# Revit family: Resideo_ThermostaticRadiatorValve_V2100Lsss
name_source: partatom
category: Pipe Accessories
units: mm (PartAtom-declared; Revit-internal decimal feet)

## family parameters
Always vertical = Yes
Cut with Voids When Loaded = No
OmniClass Number = 23.65.55.00
OmniClass Title = Distribution of Supplied Liquids/Gases
Part Type = Valve - Breaks Into
Round Connector Dimension = Use Radius
Shared = No
Work Plane-Based = No

## types (2) — shared parameters
AmbientTemperature = 0 ... 40 °C
Assembly Code = D20
AssetType = Fixed
BIMObjectName = Resideo_ThermostaticRadiatorValve_V2100L
ClassificationName = Uniclass 2015
ClassificationValue = Pr_65_54_95_89
ClosingDimension = 11.5 mm
ConnectionType = M30x1.5
DifferentialPressure = 0.1 … 0.6 bar
DocumentationCertificates = https://www.bimstore.co
DocumentationInstallationGuide = https://www.bimstore.co
DocumentationLiterature = https://www.bimstore.co
DocumentationMaintenance = https://www.bimstore.co
DocumentationTechnical = https://www.bimstore.co
DurationUnit = Year
FlowController = Yes
Force = 90 Nm
IfcExportAs = IfcValve
IfcExportType = IfcValveTypeEnum.ISOLATING
Keynote = S
Loss Method = K Coefficient
Manufacturer = Resideo
ManufacturerName = Resideo
Material = Brass
MaximumAmbientRelativeHumidity = 75 % (non condensing)
MaximumFlow = 2.7 L/min
MaximumOperatingPressure = 10.0 bar
MediaTemperatureRange = 2 ... 90 °C
MediumType = Water or water-glycol mixture according to VDI 2035
MinimumFlow = 0.2 L/min
NBSDescription = Thermostatic radiator valves
NBSObjectName = Resideo - Thermostatic radiator valves
NBSReference = 90-10-90/364
NominalDepth = 54 mm
NominalFlow = 120 kg/h
NominalHeight = 48 mm
NominalLength = 70 mm
NominalPressure = PN10
PreSetting = Yes
PrimaryMaterial = Resideo - Brass - Nickel Plated
ProductionYear = 2023
SecondaryMaterial = Resideo - Plastic - Blue
Size = 70mm (L) x 48mm (H) x 54mm (D)
StrokeStandard = 2.5 mm
URL = www.resideo.com
ValveSeries = V2100, Kombi-TRV
ValveType = V2100L
WarrantyDurationLabor = 0
WarrantyDurationParts = 0
WarrantyDurationUnit = Year
WarrantyGuarantorLabor = www.resideo.com/gb/en/contact-us/
WarrantyGuarantorParts = www.resideo.com/gb/en/contact-us/
_BSBibleVersion = 16
_CurrentRevision = 1
_DistributedBy = https://www.bimstore.co
_ObjectUserGuide = https://www.bimstore.co
pH-Range = 8 ... 9.5
zero-valued in all types: Cost, Default Elevation, ExpectedLife, K Coefficient, _BimSpecGuid

## per-type parameters (varying)
| type | ConnectionRadius | ConnectionSize | Description | ModelReference | PipeConnection | RadiatorConnection | Type Comments | a | b |
| V2100LPI10-1/2 | 5 mm  [stored 0.0164042 ft] | 10 mm  [stored 0.0328084 ft] | KOMBI-TRV, DN10, LEFT CORNER, RP1/2" | KOMBI-TRV, DN10, LEFT CORNER, RP1/2" | Rp 3/8" | R 3/8" | KOMBI-TRV, DN10, LEFT CORNER, RP1/2" | 15 mm  [stored 0.0492126 ft] | 7 mm  [stored 0.0229659 ft] |
| V2100LPI15 | 7.5 mm  [stored 0.0246063 ft] | 15 mm  [stored 0.0492126 ft] | KOMBI-TRV, DN15, LEFT CORNER, RP1/2" | KOMBI-TRV, DN15, LEFT CORNER, RP1/2" | Rp 1/2" | R 1/2" | KOMBI-TRV, DN15, LEFT CORNER, RP1/2" | 20 mm  [stored 0.0656168 ft] | 10 mm  [stored 0.0328084 ft] |

note: column(s) folded — value = type name in every type: Model, ModelNumber, TypeName

note: [stored X ft] marks values corroborated as IEEE doubles in the binary element streams (Revit-internal decimal feet)

## geometry (parser evidence)
native form markers: Sweep x2
no freeform markers — native parametric forms only
